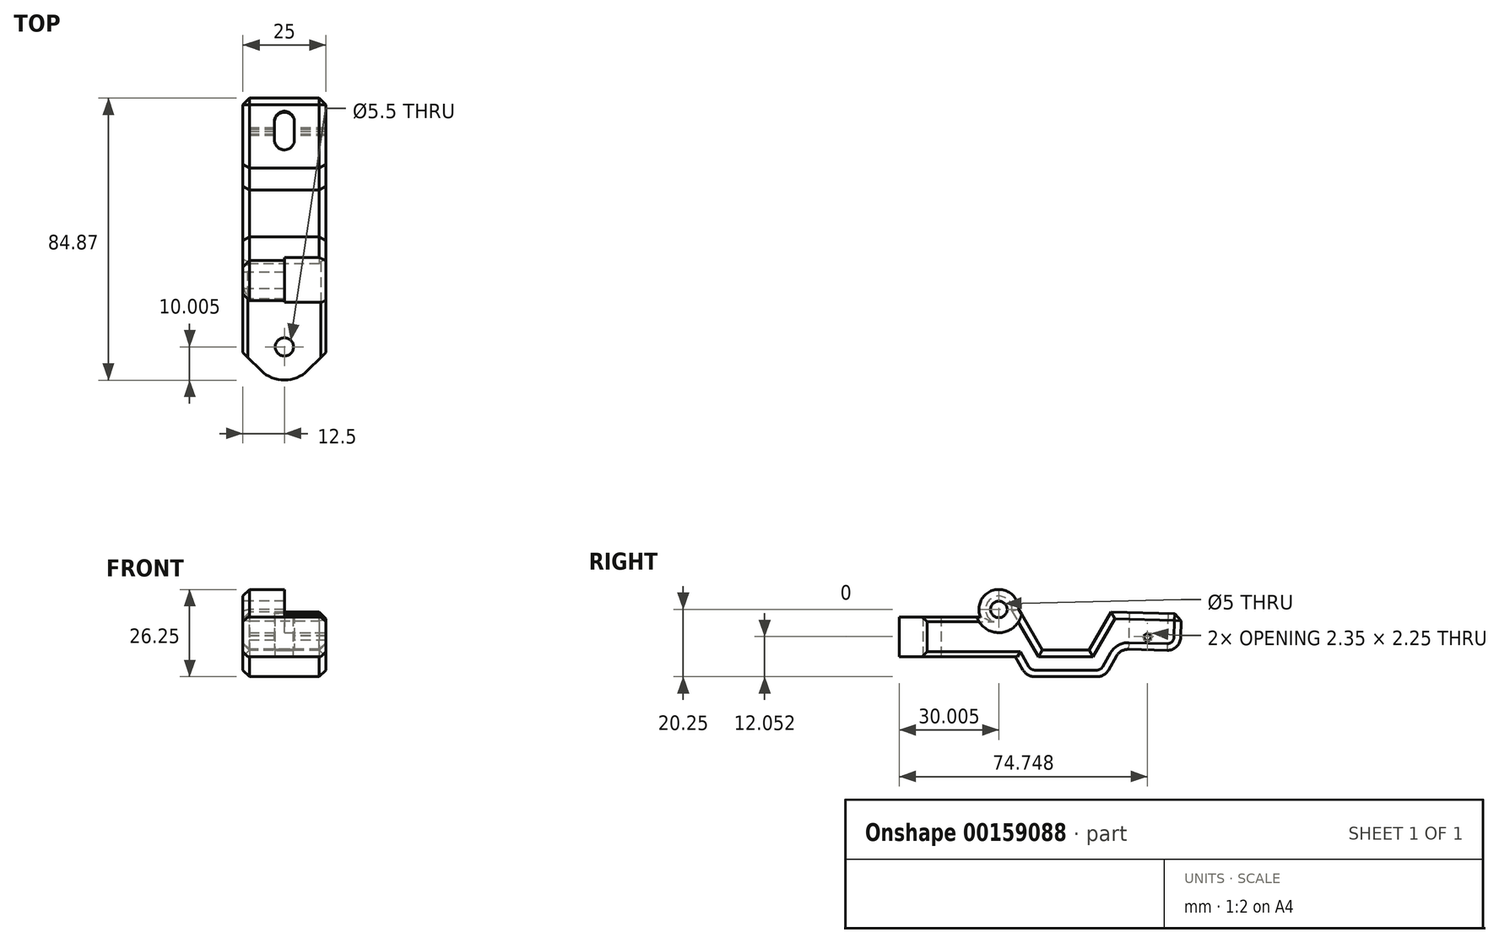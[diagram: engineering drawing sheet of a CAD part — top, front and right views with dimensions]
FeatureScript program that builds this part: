
annotation { "Feature Type Name" : "Feature", "Feature Type Description" : "" }
export const myFeature = defineFeature(function(context is Context, id is Id, definition is map)
    precondition{}
    {
        {
            var Q0;
            Q0=qCreatedBy(makeId("Right.planeOp"),FACE);
            var sketch = newSketch(context, id + "F0", { "sketchPlane" : qUnion([Q0])});
            skCircle(sketch, "E0.cCircle", {"center": v(0, 0) * mm, "radius": 12.25 * mm, "construction": true});
            skLineSegment(sketch, "E0.0", {"start": v(13.66, -0.84) * mm, "end": v(7.07, -12.25) * mm});
            skLineSegment(sketch, "E0.1", {"start": v(7.07, -12.25) * mm, "end": v(-7.07, -12.25) * mm});
            skLineSegment(sketch, "E0.2", {"start": v(-7.07, -12.25) * mm, "end": v(-14.15, 0) * mm});
            skLineSegment(sketch, "E1.2", {"start": v(15.3, -14) * mm, "end": v(12.85, -18.25) * mm});
            skLineSegment(sketch, "E1.4", {"start": v(9.38, -20.25) * mm, "end": v(-9.38, -20.25) * mm});
            skLineSegment(sketch, "E1.5", {"start": v(-12.85, -18.25) * mm, "end": v(-15.16, -14.25) * mm});
            skLineSegment(sketch, "E2.trimOffspring", {"start": v(-10.68, -6) * mm, "end": v(-10.68, -6) * mm});
            skLineSegment(sketch, "E3.trimOffspring", {"start": v(10.68, -6) * mm, "end": v(10.68, -6) * mm});
            skLineSegment(sketch, "E4.bottom", {"start": v(30.48, -12.3) * mm, "end": v(18.87, -12) * mm});
            skLineSegment(sketch, "E4.left", {"start": v(34.59, -8.41) * mm, "end": v(34.77, -1.4) * mm});
            skPoint(sketch, "E5.visualSharp", {"position": v(-11.7, -20.25) * mm});
            skArc(sketch, "E5.filletArc", {"start": v(-12.85, -18.25) * mm, "mid": v(-11.38, -19.71) * mm, "end": v(-9.38, -20.25) * mm});
            skPoint(sketch, "E6.visualSharp", {"position": v(11.7, -20.25) * mm});
            skArc(sketch, "E6.filletArc", {"start": v(9.38, -20.25) * mm, "mid": v(11.38, -19.71) * mm, "end": v(12.85, -18.25) * mm});
            skPoint(sketch, "E7.visualSharp", {"position": v(16.49, -11.94) * mm});
            skArc(sketch, "E7.filletArc", {"start": v(18.87, -12) * mm, "mid": v(16.8, -12.51) * mm, "end": v(15.3, -14) * mm});
            skPoint(sketch, "E8.visualSharp", {"position": v(34.48, -12.41) * mm});
            skArc(sketch, "E8.filletArc", {"start": v(30.48, -12.3) * mm, "mid": v(33.34, -11.2) * mm, "end": v(34.59, -8.41) * mm});
            skCircle(sketch, "E9", {"center": v(-20.15, 0) * mm, "radius": 2.5 * mm});
            skCircle(sketch, "E10", {"center": v(-20.15, 0) * mm, "radius": 6 * mm});
            skLineSegment(sketch, "E11.trimOffspring", {"start": v(13.66, -0.84) * mm, "end": v(34.77, -1.4) * mm});
            skLineSegment(sketch, "E12.bottom", {"start": v(-15.16, -14.25) * mm, "end": v(-50.15, -14.25) * mm});
            skLineSegment(sketch, "E12.right", {"start": v(-50.15, -14.25) * mm, "end": v(-50.15, -2.25) * mm});
            skLineSegment(sketch, "E13.trimOffspring", {"start": v(-25.7, -2.25) * mm, "end": v(-50.15, -2.25) * mm});
            skCircle(sketch, "E14.cCircle", {"center": v(24.59, -8.3) * mm, "radius": 1 * mm, "construction": true});
            skLineSegment(sketch, "E14.0", {"start": v(23.84, -9.29) * mm, "end": v(23.42, -7.9) * mm});
            skLineSegment(sketch, "E14.1", {"start": v(23.42, -7.9) * mm, "end": v(24.62, -7.07) * mm});
            skLineSegment(sketch, "E14.2", {"start": v(24.62, -7.07) * mm, "end": v(25.77, -7.96) * mm});
            skLineSegment(sketch, "E14.3", {"start": v(25.77, -7.96) * mm, "end": v(25.29, -9.33) * mm});
            skLineSegment(sketch, "E14.4", {"start": v(25.29, -9.33) * mm, "end": v(23.84, -9.29) * mm});
            skPoint(sketch, "E14.0.midPoint", {"position": v(23.63, -8.6) * mm});
            skSolve(sketch);
        }
        {
            var Q0;
            Q0=qSketchRegion(id+"F0",true);
            extrude(context, id + "F1", {"entities" : qUnion([Q0]), "depth" : 25 * mm});
        }
        {
            var Q0;
            Q0=makeQuery(id+"F1.opExtrude","CAP_FACE",FACE,{"disambiguationData":[OSD([sQuery(id+"F0.wireOp",EDGE,"E0.0"),sQuery(id+"F0.wireOp",EDGE,"E0.1"),sQuery(id+"F0.wireOp",EDGE,"E0.2"),sQuery(id+"F0.wireOp",EDGE,"E1.2"),sQuery(id+"F0.wireOp",EDGE,"E1.4"),sQuery(id+"F0.wireOp",EDGE,"E1.5"),sQuery(id+"F0.wireOp",EDGE,"E4.bottom"),sQuery(id+"F0.wireOp",EDGE,"E4.left"),sQuery(id+"F0.wireOp",EDGE,"E5.filletArc"),sQuery(id+"F0.wireOp",EDGE,"E6.filletArc"),sQuery(id+"F0.wireOp",EDGE,"E7.filletArc"),sQuery(id+"F0.wireOp",EDGE,"E8.filletArc"),sQuery(id+"F0.wireOp",EDGE,"E9"),sQuery(id+"F0.wireOp",EDGE,"E10"),sQuery(id+"F0.wireOp",EDGE,"E11.trimOffspring")])],"isStart":false});
            var sketch = newSketch(context, id + "F2", { "sketchPlane" : qUnion([Q0])});
            skCircle(sketch, "E15", {"center": v(-20.15, 0) * mm, "radius": 7 * mm});
            skSolve(sketch);
        }
        {
            var Q0;
            Q0=qSketchRegion(id+"F2",true);
            extrude(context, id + "F3", {"entities" : qUnion([Q0]), "operationType" : NewBodyOperationType.REMOVE, "oppositeDirection" : true, "depth" : 12.5 * mm});
        }
        {
            var Q0;
            Q0=makeQuery(id+"F1.opExtrude","SWEPT_FACE",FACE,{"disambiguationData":[OSD([sQuery(id+"F0.wireOp",EDGE,"E4.bottom")])]});
            var sketch = newSketch(context, id + "F4", { "sketchPlane" : qUnion([Q0])});
            skPoint(sketch, "E16.0.end.orphan", {"position": v(25, -19.18) * mm});
            skPoint(sketch, "E16.0.start.orphan", {"position": v(25, -30.8) * mm});
            skArc(sketch, "E17", {"start": v(9.5, -27.8) * mm, "mid": v(12.5, -30.8) * mm, "end": v(15.5, -27.8) * mm});
            skArc(sketch, "E18", {"start": v(15.5, -22.18) * mm, "mid": v(12.5, -19.18) * mm, "end": v(9.5, -22.18) * mm});
            skLineSegment(sketch, "E19", {"start": v(15.5, -22.18) * mm, "end": v(15.5, -27.8) * mm});
            skLineSegment(sketch, "E20", {"start": v(9.5, -22.18) * mm, "end": v(9.5, -27.8) * mm});
            skLineSegment(sketch, "E21.0", {"start": v(25, -34.8) * mm, "end": v(0, -34.8) * mm, "construction": true});
            skPoint(sketch, "E22", {"position": v(15.5, -24.99) * mm});
            skSolve(sketch);
        }
        {
            var Q0;
            Q0=qSketchRegion(id+"F4",true);
            extrude(context, id + "F5", {"entities" : qUnion([Q0]), "operationType" : NewBodyOperationType.REMOVE, "oppositeDirection" : true, "depth" : 25 * mm});
        }
        {
            var Q0;
            Q0=makeQuery(id+"F1.opExtrude","SWEPT_FACE",FACE,{"disambiguationData":[OSD([sQuery(id+"F0.wireOp",EDGE,"E13.trimOffspring")])]});
            var sketch = newSketch(context, id + "F6", { "sketchPlane" : qUnion([Q0])});
            skLineSegment(sketch, "E23.0", {"start": v(25, -50.15) * mm, "end": v(0, -50.15) * mm, "construction": true});
            skPoint(sketch, "E24", {"position": v(12.5, -50.15) * mm});
            skCircle(sketch, "E25", {"center": v(12.5, -40.15) * mm, "radius": 2.75 * mm});
            skArc(sketch, "E26", {"start": v(5.43, -47.22) * mm, "mid": v(12.5, -50.15) * mm, "end": v(19.57, -47.22) * mm});
            skLineSegment(sketch, "E27", {"start": v(19.57, -47.22) * mm, "end": v(34.84, -31.94) * mm});
            skLineSegment(sketch, "E28", {"start": v(5.43, -47.22) * mm, "end": v(-9.84, -31.94) * mm});
            skLineSegment(sketch, "E29.top", {"start": v(-9.84, -58.41) * mm, "end": v(34.84, -58.41) * mm});
            skLineSegment(sketch, "E29.left", {"start": v(-9.84, -31.94) * mm, "end": v(-9.84, -58.41) * mm});
            skLineSegment(sketch, "E29.right", {"start": v(34.84, -31.94) * mm, "end": v(34.84, -58.41) * mm});
            skSolve(sketch);
        }
        {
            var Q0;
            Q0 = qSketchRegion(id + "F6", true);
            extrude(context, id + "F7", {"entities" : qUnion([Q0]), "operationType" : NewBodyOperationType.REMOVE, "oppositeDirection" : true, "depth" : 25 * mm});
        }
        {
            var Q0;
            Q0=makeQuery(id+"F1.opExtrude","CAP_EDGE",EDGE,{"disambiguationData":[OSD([sQuery(id+"F0.wireOp",EDGE,"E11.trimOffspring")])],"isStart":true});
            var Q1;
            Q1=makeQuery(id+"F1.opExtrude","CAP_EDGE",EDGE,{"disambiguationData":[OSD([sQuery(id+"F0.wireOp",EDGE,"E0.0")])],"isStart":true});
            var Q2;
            Q2=makeQuery(id+"F1.opExtrude","CAP_EDGE",EDGE,{"disambiguationData":[OSD([sQuery(id+"F0.wireOp",EDGE,"E0.1")])],"isStart":true});
            var Q3;
            Q3=makeQuery(id+"F1.opExtrude","CAP_EDGE",EDGE,{"disambiguationData":[OSD([sQuery(id+"F0.wireOp",EDGE,"E0.2")])],"isStart":true});
            var Q4;
            Q4=makeQuery(id+"F1.opExtrude","CAP_EDGE",EDGE,{"disambiguationData":[OSD([sQuery(id+"F0.wireOp",EDGE,"E10")])],"isStart":true});
            var Q5;
            Q5=makeQuery(id+"F1.opExtrude","CAP_EDGE",EDGE,{"disambiguationData":[OSD([sQuery(id+"F0.wireOp",EDGE,"E1.5")])],"isStart":true});
            var Q6;
            Q6=makeQuery(id+"F1.opExtrude","SWEPT_EDGE",EDGE,{"disambiguationData":[OSD([sQuery(id+"F0.wireOp",EDGE,"E4.left"),sQuery(id+"F0.wireOp",EDGE,"E11.trimOffspring")])]});
            var Q7;
            Q7=makeQuery(id+"F1.opExtrude","CAP_EDGE",EDGE,{"disambiguationData":[OSD([sQuery(id+"F0.wireOp",EDGE,"E11.trimOffspring")])],"isStart":false});
            var Q8;
            Q8=makeQuery(id+"F1.opExtrude","CAP_EDGE",EDGE,{"disambiguationData":[OSD([sQuery(id+"F0.wireOp",EDGE,"E0.0")])],"isStart":false});
            var Q9;
            Q9=makeQuery(id+"F1.opExtrude","CAP_EDGE",EDGE,{"disambiguationData":[OSD([sQuery(id+"F0.wireOp",EDGE,"E0.1")])],"isStart":false});
            var Q10;
            Q10=makeQuery(id+"F1.opExtrude","CAP_EDGE",EDGE,{"disambiguationData":[OSD([sQuery(id+"F0.wireOp",EDGE,"E0.2")])],"isStart":false});
            var Q11;
            Q11=makeQuery(id+"F1.opExtrude","CAP_EDGE",EDGE,{"disambiguationData":[OSD([sQuery(id+"F0.wireOp",EDGE,"E1.5")])],"isStart":false});
            var Q12;
            Q12=makeQuery(id+"F1.opExtrude","CAP_EDGE",EDGE,{"disambiguationData":[OSD([sQuery(id+"F0.wireOp",EDGE,"E5.filletArc")])],"isStart":false});
            var Q13;
            Q13=makeQuery(id+"F1.opExtrude","CAP_EDGE",EDGE,{"disambiguationData":[OSD([sQuery(id+"F0.wireOp",EDGE,"E1.4")])],"isStart":false});
            var Q14;
            Q14=makeQuery(id+"F1.opExtrude","CAP_EDGE",EDGE,{"disambiguationData":[OSD([sQuery(id+"F0.wireOp",EDGE,"E6.filletArc")])],"isStart":false});
            var Q15;
            Q15=makeQuery(id+"F1.opExtrude","CAP_EDGE",EDGE,{"disambiguationData":[OSD([sQuery(id+"F0.wireOp",EDGE,"E1.2")])],"isStart":false});
            var Q16;
            Q16=makeQuery(id+"F1.opExtrude","CAP_EDGE",EDGE,{"disambiguationData":[OSD([sQuery(id+"F0.wireOp",EDGE,"E4.bottom")])],"isStart":false});
            var Q17;
            Q17=makeQuery(id+"F1.opExtrude","CAP_EDGE",EDGE,{"disambiguationData":[OSD([sQuery(id+"F0.wireOp",EDGE,"E7.filletArc")])],"isStart":false});
            var Q18;
            Q18=makeQuery(id+"F1.opExtrude","CAP_EDGE",EDGE,{"disambiguationData":[OSD([sQuery(id+"F0.wireOp",EDGE,"E8.filletArc")])],"isStart":false});
            var Q19;
            Q19=makeQuery(id+"F1.opExtrude","CAP_EDGE",EDGE,{"disambiguationData":[OSD([sQuery(id+"F0.wireOp",EDGE,"E4.left")])],"isStart":false});
            var Q20;
            Q20=makeQuery(id+"F1.opExtrude","CAP_EDGE",EDGE,{"disambiguationData":[OSD([sQuery(id+"F0.wireOp",EDGE,"E5.filletArc")])],"isStart":true});
            var Q21;
            Q21=makeQuery(id+"F1.opExtrude","CAP_EDGE",EDGE,{"disambiguationData":[OSD([sQuery(id+"F0.wireOp",EDGE,"E1.4")])],"isStart":true});
            var Q22;
            Q22=makeQuery(id+"F1.opExtrude","CAP_EDGE",EDGE,{"disambiguationData":[OSD([sQuery(id+"F0.wireOp",EDGE,"E6.filletArc")])],"isStart":true});
            var Q23;
            Q23=makeQuery(id+"F1.opExtrude","CAP_EDGE",EDGE,{"disambiguationData":[OSD([sQuery(id+"F0.wireOp",EDGE,"E1.2")])],"isStart":true});
            var Q24;
            Q24=makeQuery(id+"F1.opExtrude","CAP_EDGE",EDGE,{"disambiguationData":[OSD([sQuery(id+"F0.wireOp",EDGE,"E7.filletArc")])],"isStart":true});
            var Q25;
            Q25=makeQuery(id+"F1.opExtrude","CAP_EDGE",EDGE,{"disambiguationData":[OSD([sQuery(id+"F0.wireOp",EDGE,"E4.bottom")])],"isStart":true});
            var Q26;
            Q26=makeQuery(id+"F1.opExtrude","CAP_EDGE",EDGE,{"disambiguationData":[OSD([sQuery(id+"F0.wireOp",EDGE,"E8.filletArc")])],"isStart":true});
            var Q27;
            Q27=makeQuery(id+"F1.opExtrude","CAP_EDGE",EDGE,{"disambiguationData":[OSD([sQuery(id+"F0.wireOp",EDGE,"E4.left")])],"isStart":true});
            chamfer(context, id + "F8", {"entities" : qUnion([Q0, Q1, Q2, Q3, Q4, Q5, Q6, Q7, Q8, Q9, Q10, Q11, Q12, Q13, Q14, Q15, Q16, Q17, Q18, Q19, Q20, Q21, Q22, Q23, Q24, Q25, Q26, Q27]), "width" : 2 * mm, "tangentPropagation" : true});
        }
        {
            var Q0;
            Q0=makeQuery(id+"F1.opExtrude","CAP_EDGE",EDGE,{"disambiguationData":[OSD([sQuery(id+"F0.wireOp",EDGE,"E12.bottom")])],"isStart":false});
            var Q1;
            Q1=makeQuery(id+"F1.opExtrude","CAP_EDGE",EDGE,{"disambiguationData":[OSD([sQuery(id+"F0.wireOp",EDGE,"E13.trimOffspring")])],"isStart":false});
            var Q2;
            Q2=makeQuery(id+"F1.opExtrude","CAP_EDGE",EDGE,{"disambiguationData":[OSD([sQuery(id+"F0.wireOp",EDGE,"E13.trimOffspring")])],"isStart":true});
            var Q3;
            Q3=makeQuery(id+"F1.opExtrude","CAP_EDGE",EDGE,{"disambiguationData":[OSD([sQuery(id+"F0.wireOp",EDGE,"E12.bottom")])],"isStart":true});
            chamfer(context, id + "F9", {"entities" : qUnion([Q0, Q1, Q2, Q3]), "width" : 1.5 * mm, "tangentPropagation" : true});
        }
    });
